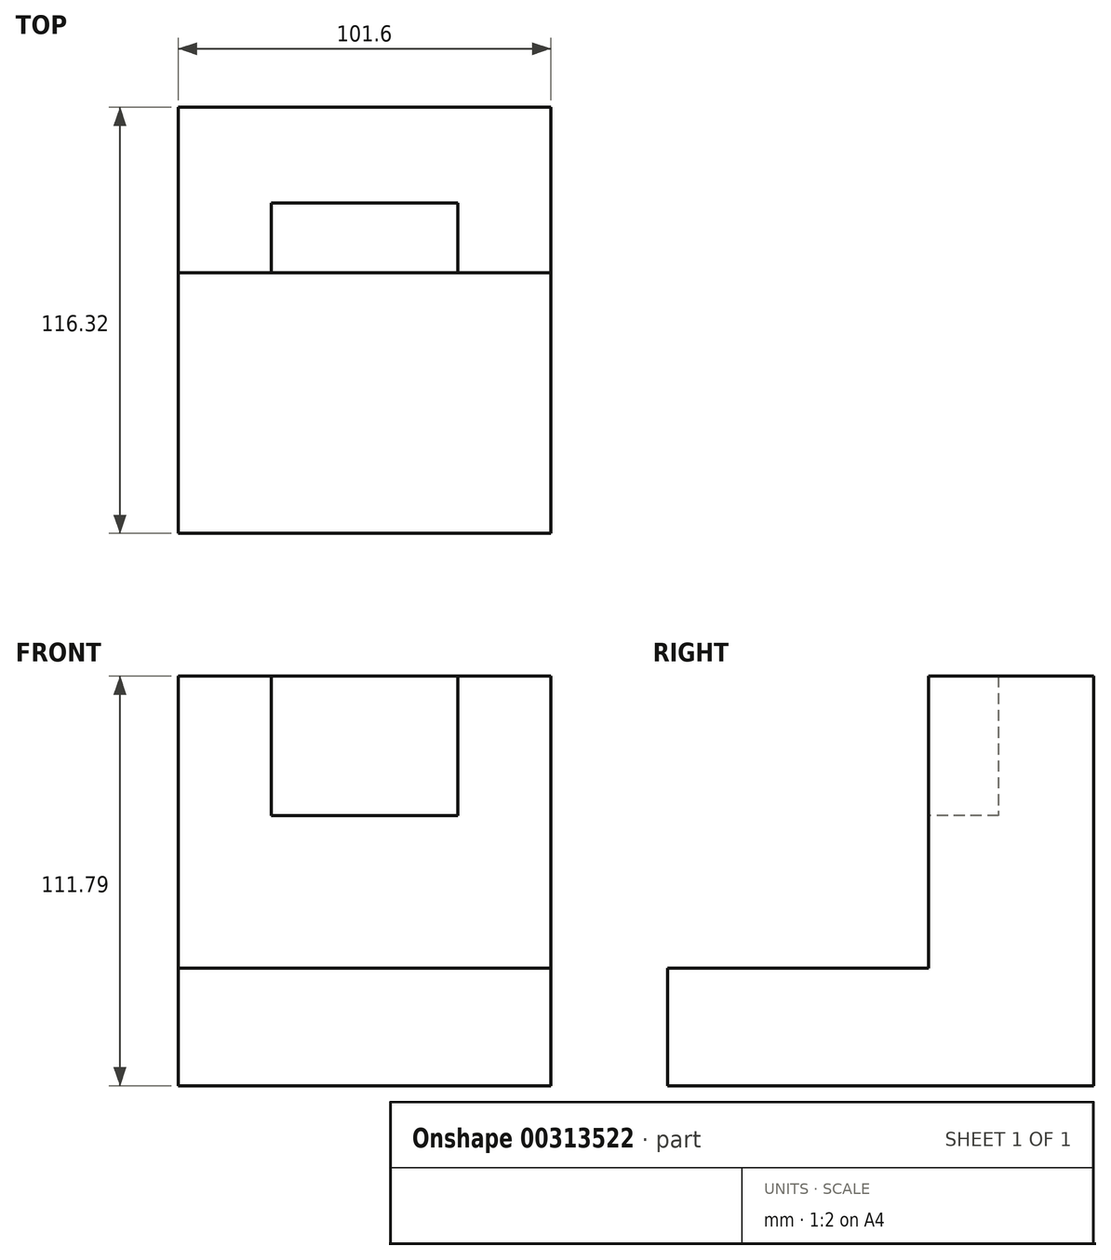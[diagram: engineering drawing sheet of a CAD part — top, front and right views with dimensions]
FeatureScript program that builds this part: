
annotation { "Feature Type Name" : "Feature", "Feature Type Description" : "" }
export const myFeature = defineFeature(function(context is Context, id is Id, definition is map)
    precondition{}
    {
        {
            var Q0;
            Q0=qCreatedBy(makeId("Right.planeOp"),FACE);
            var sketch = newSketch(context, id + "F0", { "sketchPlane" : qUnion([Q0])});
            skLineSegment(sketch, "E0", {"start": v(-65.11, -18.16) * mm, "end": v(-65.11, -50.22) * mm});
            skLineSegment(sketch, "E1", {"start": v(-65.11, -50.22) * mm, "end": v(51.21, -50.22) * mm});
            skLineSegment(sketch, "E2", {"start": v(51.21, -50.22) * mm, "end": v(51.21, 61.57) * mm});
            skLineSegment(sketch, "E3", {"start": v(51.21, 61.57) * mm, "end": v(6.1, 61.57) * mm});
            skLineSegment(sketch, "E4", {"start": v(6.1, 61.57) * mm, "end": v(6.1, -18.16) * mm});
            skLineSegment(sketch, "E5", {"start": v(6.1, -18.16) * mm, "end": v(-65.11, -18.16) * mm});
            skSolve(sketch);
        }
        {
            var Q0;
            Q0=makeQuery(id+"F0.imprint","IMPRINT",FACE,{"disambiguationData":[TD([[makeQuery(id+"F0.imprint","IMPRINT",EDGE,{"derivedFrom":sQuery(id+"F0.wireOp",EDGE,"E0")}),1.0]])]});
            extrude(context, id + "F1", {"entities" : qUnion([Q0]), "oppositeDirection" : true, "depth" : 101.6 * mm});
        }
        {
            var Q0;
            Q0=makeQuery(id+"F1.opExtrude","SWEPT_FACE",FACE,{"disambiguationData":[OSD([sQuery(id+"F0.wireOp",EDGE,"E4")])]});
            var sketch = newSketch(context, id + "F2", { "sketchPlane" : qUnion([Q0])});
            skLineSegment(sketch, "E6.bottom", {"start": v(-76.2, 61.57) * mm, "end": v(-25.4, 61.57) * mm});
            skLineSegment(sketch, "E6.top", {"start": v(-76.2, 23.47) * mm, "end": v(-25.4, 23.47) * mm});
            skLineSegment(sketch, "E6.left", {"start": v(-76.2, 61.57) * mm, "end": v(-76.2, 23.47) * mm});
            skLineSegment(sketch, "E6.right", {"start": v(-25.4, 61.57) * mm, "end": v(-25.4, 23.47) * mm});
            skLineSegment(sketch, "E7", {"start": v(-101.6, 61.57) * mm, "end": v(-76.2, 61.57) * mm});
            skLineSegment(sketch, "E8", {"start": v(-25.4, 61.57) * mm, "end": v(-25.4, 53.06) * mm});
            skLineSegment(sketch, "E9", {"start": v(-25.4, 61.57) * mm, "end": v(0, 61.57) * mm});
            skSolve(sketch);
        }
        {
            var Q0;
            Q0=makeQuery(id+"F2.imprint","IMPRINT",FACE,{"disambiguationData":[TD([[makeQuery(id+"F2.imprint","IMPRINT",EDGE,{"derivedFrom":sQuery(id+"F2.wireOp",EDGE,"E6.bottom")}),-1.0]])]});
            extrude(context, id + "F3", {"entities" : qUnion([Q0]), "operationType" : NewBodyOperationType.REMOVE, "oppositeDirection" : true, "depth" : 19.05 * mm});
        }
    });
